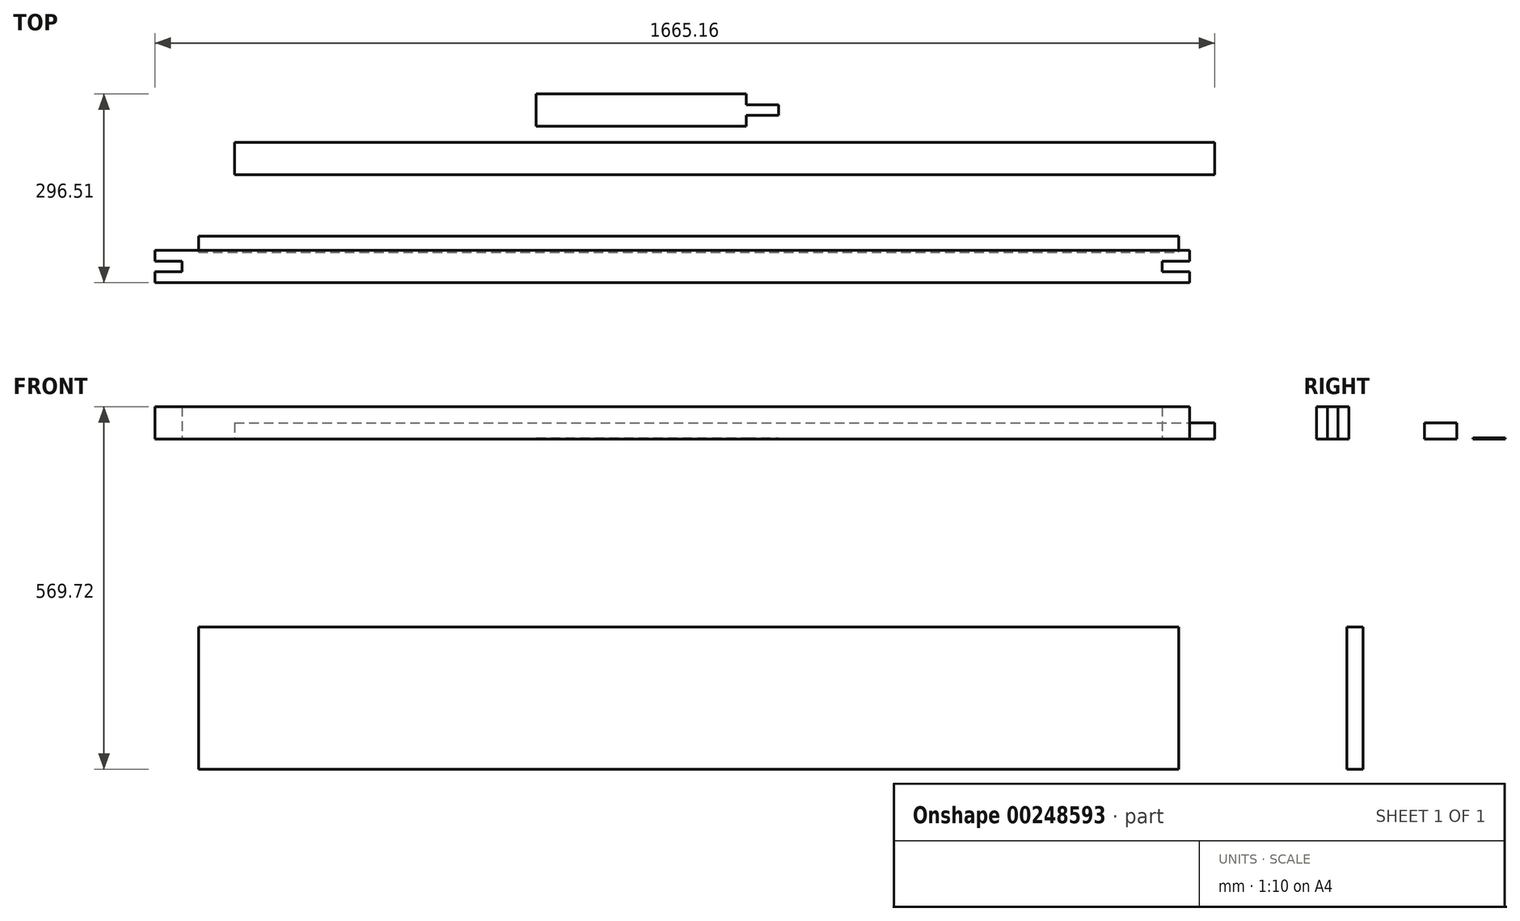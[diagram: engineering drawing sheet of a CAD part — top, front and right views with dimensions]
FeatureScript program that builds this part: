
annotation { "Feature Type Name" : "Feature", "Feature Type Description" : "" }
export const myFeature = defineFeature(function(context is Context, id is Id, definition is map)
    precondition{}
    {
        {
            var Q0;
            Q0=qCreatedBy(makeId("Top.planeOp"),FACE);
            var sketch = newSketch(context, id + "F0", { "sketchPlane" : qUnion([Q0])});
            skLineSegment(sketch, "E0", {"start": v(-811.94, -39.2) * mm, "end": v(-811.94, -22.26) * mm});
            skLineSegment(sketch, "E1", {"start": v(-811.94, -22.26) * mm, "end": v(813.66, -22.26) * mm});
            skLineSegment(sketch, "E2", {"start": v(813.66, -22.26) * mm, "end": v(813.66, -39.2) * mm});
            skLineSegment(sketch, "E3", {"start": v(813.66, -39.2) * mm, "end": v(770.8, -39.2) * mm});
            skLineSegment(sketch, "E4", {"start": v(770.8, -39.2) * mm, "end": v(770.8, -56.13) * mm});
            skLineSegment(sketch, "E5", {"start": v(770.8, -56.13) * mm, "end": v(813.66, -56.13) * mm});
            skLineSegment(sketch, "E6", {"start": v(813.66, -56.13) * mm, "end": v(813.66, -73.06) * mm});
            skLineSegment(sketch, "E7", {"start": v(813.66, -73.06) * mm, "end": v(-811.94, -73.06) * mm});
            skLineSegment(sketch, "E8", {"start": v(-811.94, -73.06) * mm, "end": v(-811.94, -56.13) * mm});
            skLineSegment(sketch, "E9", {"start": v(-811.94, -56.13) * mm, "end": v(-769.08, -56.13) * mm});
            skLineSegment(sketch, "E10", {"start": v(-769.08, -56.13) * mm, "end": v(-769.08, -39.2) * mm});
            skLineSegment(sketch, "E11", {"start": v(-769.08, -39.2) * mm, "end": v(-811.94, -39.2) * mm});
            skSolve(sketch);
        }
        {
            var Q0;
            Q0=makeQuery(id+"F0.imprint","IMPRINT",FACE,{"disambiguationData":[TD([[makeQuery(id+"F0.imprint","IMPRINT",EDGE,{"derivedFrom":sQuery(id+"F0.wireOp",EDGE,"E0")}),-1.0]])]});
            extrude(context, id + "F1", {"entities" : qUnion([Q0]), "depth" : 50.8 * mm});
        }
        {
            var Q0;
            Q0=qCreatedBy(makeId("Front.planeOp"),FACE);
            var sketch = newSketch(context, id + "F2", { "sketchPlane" : qUnion([Q0])});
            skLineSegment(sketch, "E12.bottom", {"start": v(-743.52, -295.08) * mm, "end": v(796.35, -295.08) * mm});
            skLineSegment(sketch, "E12.top", {"start": v(-743.52, -518.92) * mm, "end": v(796.35, -518.92) * mm});
            skLineSegment(sketch, "E12.left", {"start": v(-743.52, -295.08) * mm, "end": v(-743.52, -518.92) * mm});
            skLineSegment(sketch, "E12.right", {"start": v(796.35, -295.08) * mm, "end": v(796.35, -518.92) * mm});
            skSolve(sketch);
        }
        {
            var Q0;
            Q0 = qSketchRegion(id + "F2", true);
            extrude(context, id + "F3", {"entities" : qUnion([Q0]), "depth" : 25.4 * mm});
        }
        {
            var Q0;
            Q0=qCreatedBy(makeId("Top.planeOp"),FACE);
            var sketch = newSketch(context, id + "F4", { "sketchPlane" : qUnion([Q0])});
            skLineSegment(sketch, "E13", {"start": v(-212.82, 223.45) * mm, "end": v(117.38, 223.45) * mm});
            skLineSegment(sketch, "E14", {"start": v(117.38, 206.52) * mm, "end": v(168.18, 206.52) * mm});
            skLineSegment(sketch, "E15", {"start": v(168.18, 206.52) * mm, "end": v(168.18, 189.59) * mm});
            skLineSegment(sketch, "E16", {"start": v(168.18, 189.59) * mm, "end": v(117.38, 189.59) * mm});
            skLineSegment(sketch, "E17", {"start": v(117.38, 189.59) * mm, "end": v(117.38, 172.65) * mm});
            skLineSegment(sketch, "E18", {"start": v(117.38, 172.65) * mm, "end": v(-212.82, 172.65) * mm});
            skLineSegment(sketch, "E19", {"start": v(-212.82, 172.65) * mm, "end": v(-212.82, 223.45) * mm});
            skLineSegment(sketch, "E20", {"start": v(117.38, 223.45) * mm, "end": v(117.38, 206.52) * mm});
            skSolve(sketch);
        }
        {
            var Q0;
            Q0=makeQuery(id+"F4.imprint","IMPRINT",FACE,{"disambiguationData":[TD([[makeQuery(id+"F4.imprint","IMPRINT",EDGE,{"derivedFrom":sQuery(id+"F4.wireOp",EDGE,"E13")}),-1.0]])]});
            extrude(context, id + "F5", {"entities" : qUnion([Q0]), "depth" : (1 + (11 / 16)) * mm});
        }
        {
            var Q0;
            Q0=qCreatedBy(makeId("Top.planeOp"),FACE);
            var sketch = newSketch(context, id + "F6", { "sketchPlane" : qUnion([Q0])});
            skLineSegment(sketch, "E21.bottom", {"start": v(-686.65, 147.06) * mm, "end": v(853.22, 147.06) * mm});
            skLineSegment(sketch, "E21.top", {"start": v(-686.65, 96.26) * mm, "end": v(853.22, 96.26) * mm});
            skLineSegment(sketch, "E21.left", {"start": v(-686.65, 147.06) * mm, "end": v(-686.65, 96.26) * mm});
            skLineSegment(sketch, "E21.right", {"start": v(853.22, 147.06) * mm, "end": v(853.22, 96.26) * mm});
            skSolve(sketch);
        }
        {
            var Q0;
            Q0=makeQuery(id+"F6.imprint","IMPRINT",FACE,{"disambiguationData":[TD([[makeQuery(id+"F6.imprint","IMPRINT",EDGE,{"derivedFrom":sQuery(id+"F6.wireOp",EDGE,"E21.bottom")}),-1.0]])]});
            extrude(context, id + "F7", {"entities" : qUnion([Q0]), "depth" : 25.4 * mm});
        }
    });
